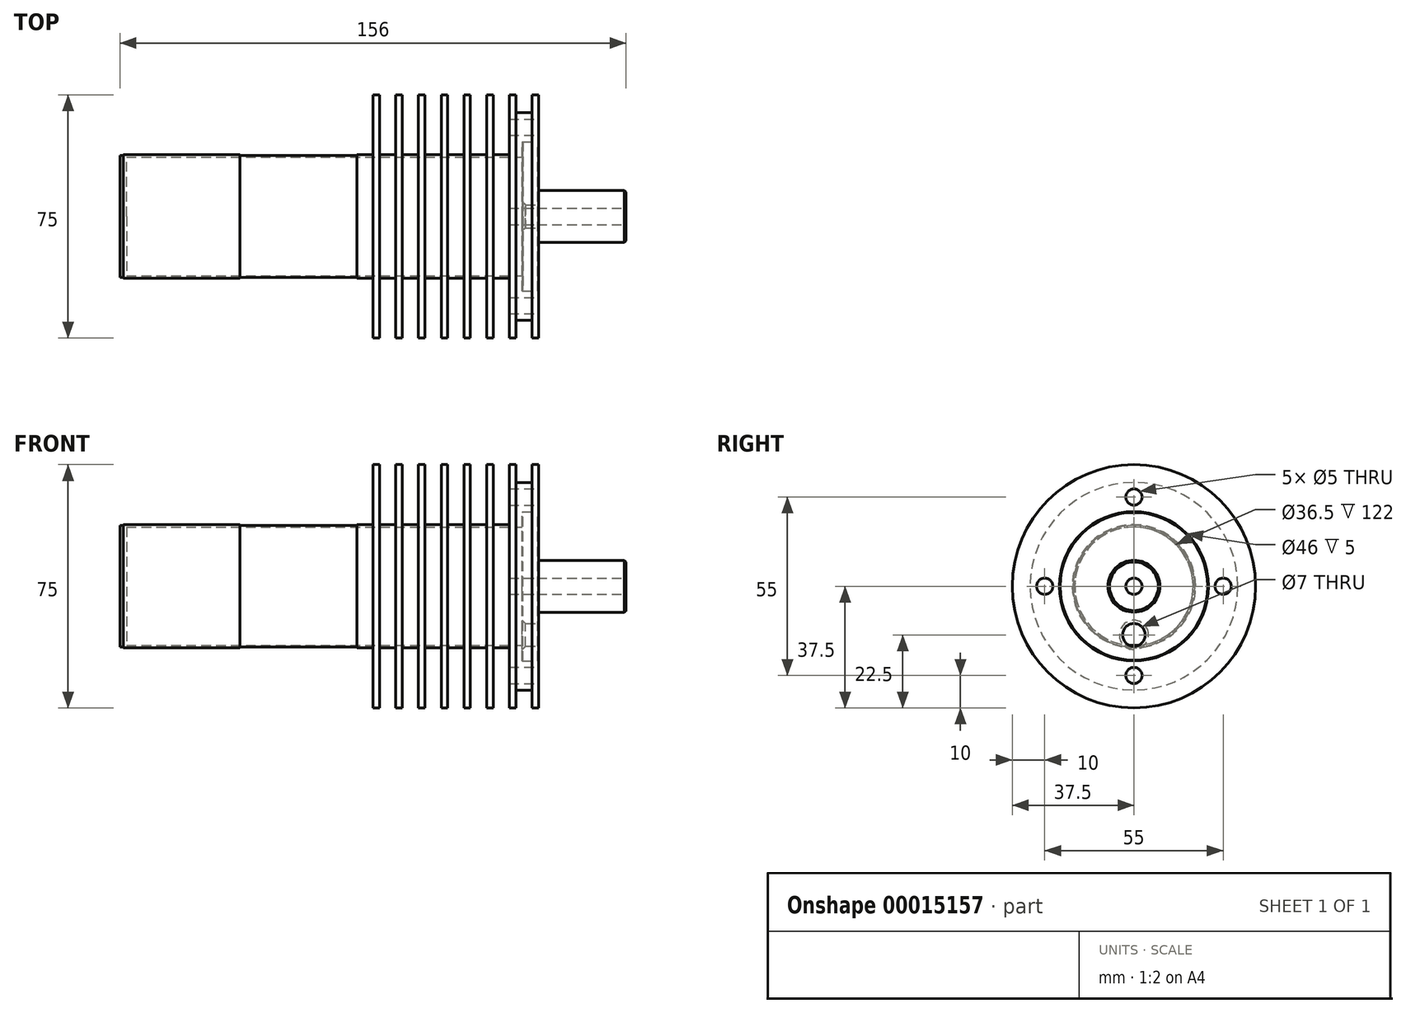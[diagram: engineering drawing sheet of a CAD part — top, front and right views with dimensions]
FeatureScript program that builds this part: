
annotation { "Feature Type Name" : "Feature", "Feature Type Description" : "" }
export const myFeature = defineFeature(function(context is Context, id is Id, definition is map)
    precondition{}
    {
        {
            var Q0;
            Q0=qCreatedBy(makeId("Front.planeOp"),FACE);
            var sketch = newSketch(context, id + "F0", { "sketchPlane" : qUnion([Q0])});
            skLineSegment(sketch, "E0.bottom", {"start": v(0, 0) * mm, "end": v(-128, 0) * mm});
            skLineSegment(sketch, "E0.top", {"start": v(-5, 18.25) * mm, "end": v(-56, 18.25) * mm});
            skLineSegment(sketch, "E0.left", {"start": v(0, 0) * mm, "end": v(0, 18.25) * mm, "construction": true});
            skLineSegment(sketch, "E0.right", {"start": v(-128, 0) * mm, "end": v(-128, 18.25) * mm, "construction": true});
            skLineSegment(sketch, "E1.top", {"start": v(-128, 19) * mm, "end": v(-92, 19) * mm});
            skLineSegment(sketch, "E1.left", {"start": v(-128, 18.25) * mm, "end": v(-128, 19) * mm});
            skLineSegment(sketch, "E1.right", {"start": v(-92, 18.75) * mm, "end": v(-92, 19) * mm});
            skLineSegment(sketch, "E2.bottom", {"start": v(-92, 18.25) * mm, "end": v(-56, 18.25) * mm});
            skLineSegment(sketch, "E2.top", {"start": v(-92, 18.75) * mm, "end": v(-56, 18.75) * mm});
            skLineSegment(sketch, "E3", {"start": v(-92, 18.25) * mm, "end": v(-128, 18.25) * mm});
            skLineSegment(sketch, "E4", {"start": v(-56, 19) * mm, "end": v(-51, 19) * mm});
            skLineSegment(sketch, "E5", {"start": v(-56, 18.75) * mm, "end": v(-56, 19) * mm});
            skLineSegment(sketch, "E6.bottom", {"start": v(-5, 18.25) * mm, "end": v(-51, 18.25) * mm});
            skLineSegment(sketch, "E6.top", {"start": v(0, 37.5) * mm, "end": v(-2, 37.5) * mm});
            skLineSegment(sketch, "E6.left", {"start": v(0, 23) * mm, "end": v(0, 37.5) * mm});
            skLineSegment(sketch, "E7", {"start": v(-9, 37.5) * mm, "end": v(-9, 19) * mm});
            skLineSegment(sketch, "E8.top", {"start": v(-7, 32) * mm, "end": v(-2, 32) * mm});
            skLineSegment(sketch, "E8.left", {"start": v(-7, 37.5) * mm, "end": v(-7, 32) * mm});
            skLineSegment(sketch, "E8.right", {"start": v(-2, 37.5) * mm, "end": v(-2, 32) * mm});
            skLineSegment(sketch, "E9.top", {"start": v(0, 23) * mm, "end": v(-5, 23) * mm});
            skLineSegment(sketch, "E9.right", {"start": v(-5, 18.25) * mm, "end": v(-5, 23) * mm});
            skLineSegment(sketch, "E10.bottom", {"start": v(-14, 37.5) * mm, "end": v(-16, 37.5) * mm});
            skLineSegment(sketch, "E10.left", {"start": v(-14, 37.5) * mm, "end": v(-14, 19) * mm});
            skLineSegment(sketch, "E10.right", {"start": v(-16, 37.5) * mm, "end": v(-16, 19) * mm});
            skLineSegment(sketch, "E11.1.0.0", {"start": v(-21, 37.5) * mm, "end": v(-21, 19) * mm});
            skLineSegment(sketch, "E11.1.0.1", {"start": v(-23, 37.5) * mm, "end": v(-23, 19) * mm});
            skLineSegment(sketch, "E11.2.0.0", {"start": v(-28, 37.5) * mm, "end": v(-28, 19) * mm});
            skLineSegment(sketch, "E11.2.0.1", {"start": v(-30, 37.5) * mm, "end": v(-30, 19) * mm});
            skLineSegment(sketch, "E11.3.0.0", {"start": v(-35, 37.5) * mm, "end": v(-35, 19) * mm});
            skLineSegment(sketch, "E11.3.0.1", {"start": v(-37, 37.5) * mm, "end": v(-37, 19) * mm});
            skLineSegment(sketch, "E11.4.0.0", {"start": v(-42, 37.5) * mm, "end": v(-42, 19) * mm});
            skLineSegment(sketch, "E11.4.0.1", {"start": v(-44, 37.5) * mm, "end": v(-44, 19) * mm});
            skLineSegment(sketch, "E11.5.0.0", {"start": v(-49, 37.5) * mm, "end": v(-49, 19) * mm});
            skLineSegment(sketch, "E11.5.0.1", {"start": v(-51, 37.5) * mm, "end": v(-51, 19) * mm});
            skLineSegment(sketch, "E11.direction1", {"start": v(-16, 19) * mm, "end": v(-21, 19) * mm, "construction": true});
            skLineSegment(sketch, "E12", {"start": v(0, 27.5) * mm, "end": v(-9, 27.5) * mm, "construction": true});
            skLineSegment(sketch, "E13.0", {"start": v(0, 30) * mm, "end": v(-9, 30) * mm, "construction": true});
            skLineSegment(sketch, "E14.0", {"start": v(0, 25) * mm, "end": v(-9, 25) * mm, "construction": true});
            skLineSegment(sketch, "E15.trimOffspring", {"start": v(-7, 37.5) * mm, "end": v(-9, 37.5) * mm});
            skLineSegment(sketch, "E16.trimOffspring", {"start": v(-21, 37.5) * mm, "end": v(-23, 37.5) * mm});
            skLineSegment(sketch, "E17.trimOffspring", {"start": v(-28, 37.5) * mm, "end": v(-30, 37.5) * mm});
            skLineSegment(sketch, "E18.trimOffspring", {"start": v(-35, 37.5) * mm, "end": v(-37, 37.5) * mm});
            skLineSegment(sketch, "E19.trimOffspring", {"start": v(-42, 37.5) * mm, "end": v(-44, 37.5) * mm});
            skLineSegment(sketch, "E20.trimOffspring", {"start": v(-49, 37.5) * mm, "end": v(-51, 37.5) * mm});
            skLineSegment(sketch, "E21.trimOffspring", {"start": v(-21, 19) * mm, "end": v(-16, 19) * mm});
            skLineSegment(sketch, "E22.trimOffspring", {"start": v(-28, 19) * mm, "end": v(-23, 19) * mm});
            skLineSegment(sketch, "E23.trimOffspring", {"start": v(-35, 19) * mm, "end": v(-30, 19) * mm});
            skLineSegment(sketch, "E24.trimOffspring", {"start": v(-42, 19) * mm, "end": v(-37, 19) * mm});
            skLineSegment(sketch, "E25.trimOffspring", {"start": v(-49, 19) * mm, "end": v(-44, 19) * mm});
            skLineSegment(sketch, "E26.trimOffspring", {"start": v(-14, 19) * mm, "end": v(-9, 19) * mm});
            skPoint(sketch, "E27.orphan", {"position": v(-91, 19) * mm});
            skPoint(sketch, "E28.orphan", {"position": v(-84, 19) * mm});
            skPoint(sketch, "E29.orphan", {"position": v(-77, 19) * mm});
            skPoint(sketch, "E30.orphan", {"position": v(-70, 19) * mm});
            skPoint(sketch, "E31.orphan", {"position": v(-63, 19) * mm});
            skLineSegment(sketch, "E32", {"start": v(-5, 18.25) * mm, "end": v(0, 18.25) * mm, "construction": true});
            skSolve(sketch);
        }
        {
            var Q0;
            Q0=makeQuery(id+"F0.imprint","IMPRINT",FACE,{"disambiguationData":[TD([[makeQuery(id+"F0.imprint","IMPRINT",EDGE,{"derivedFrom":sQuery(id+"F0.wireOp",EDGE,"E0.top")}),-1.0]])]});
            var Q1;
            Q1=sQuery(id+"F0.wireOp",EDGE,"E0.bottom");
            revolve(context, id + "F1", {"entities" : qUnion([Q0]), "axis" : qUnion([Q1]), "revolveType" : RevolveType.FULL});
        }
        {
            var Q0;
            Q0=makeQuery(id+"F1.opRevolve","SWEPT_FACE",FACE,{"disambiguationData":[OSD([sQuery(id+"F0.wireOp",EDGE,"E6.left")])]});
            var sketch = newSketch(context, id + "F2", { "sketchPlane" : qUnion([Q0])});
            skPoint(sketch, "E33.0", {"position": v(0, 0) * mm});
            skCircle(sketch, "E34", {"center": v(0, 0) * mm, "radius": 27.5 * mm, "construction": true});
            skLineSegment(sketch, "E35", {"start": v(0, 0) * mm, "end": v(27.5, 0) * mm, "construction": true});
            skCircle(sketch, "E36", {"center": v(27.5, 0) * mm, "radius": 2.5 * mm});
            skCircle(sketch, "E37.1.0", {"center": v(0, 27.5) * mm, "radius": 2.5 * mm});
            skCircle(sketch, "E37.2.0", {"center": v(-27.5, 0) * mm, "radius": 2.5 * mm});
            skCircle(sketch, "E37.3.0", {"center": v(0, -27.5) * mm, "radius": 2.5 * mm});
            skSolve(sketch);
        }
        {
            var Q0;
            Q0=makeQuery(id+"F2.imprint","IMPRINT",FACE,{"disambiguationData":[TD([[makeQuery(id+"F2.imprint","IMPRINT",EDGE,{"derivedFrom":sQuery(id+"F2.wireOp",EDGE,"E37.1.0")}),1.0]])]});
            var Q1;
            Q1=makeQuery(id+"F2.imprint","IMPRINT",FACE,{"disambiguationData":[TD([[makeQuery(id+"F2.imprint","IMPRINT",EDGE,{"derivedFrom":sQuery(id+"F2.wireOp",EDGE,"E36")}),1.0]])]});
            var Q2;
            Q2=makeQuery(id+"F2.imprint","IMPRINT",FACE,{"disambiguationData":[TD([[makeQuery(id+"F2.imprint","IMPRINT",EDGE,{"derivedFrom":sQuery(id+"F2.wireOp",EDGE,"E37.3.0")}),1.0]])]});
            var Q3;
            Q3=makeQuery(id+"F2.imprint","IMPRINT",FACE,{"disambiguationData":[TD([[makeQuery(id+"F2.imprint","IMPRINT",EDGE,{"derivedFrom":sQuery(id+"F2.wireOp",EDGE,"E37.2.0")}),1.0]])]});
            var Q4;
            Q4=makeQuery(id+"F1.opRevolve","SWEPT_FACE",FACE,{"disambiguationData":[OSD([sQuery(id+"F0.wireOp",EDGE,"E7")])]});
            extrude(context, id + "F3", {"entities" : qUnion([Q0, Q1, Q2, Q3]), "operationType" : NewBodyOperationType.REMOVE, "endBound" : BoundingType.UP_TO_SURFACE, "oppositeDirection" : true, "endBoundEntityFace" : qUnion([Q4]), "depth" : 25 * mm});
        }
        {
            var Q0;
            Q0=makeQuery(id+"F1.opRevolve","SWEPT_FACE",FACE,{"disambiguationData":[OSD([sQuery(id+"F0.wireOp",EDGE,"E1.left")])]});
            var sketch = newSketch(context, id + "F4", { "sketchPlane" : qUnion([Q0])});
            skCircle(sketch, "E38.0", {"center": v(0, 0) * mm, "radius": 18.25 * mm});
            skCircle(sketch, "E39", {"center": v(0, 0) * mm, "radius": 18.75 * mm});
            skSolve(sketch);
        }
        {
            var Q0;
            Q0=makeQuery(id+"F4.imprint","IMPRINT",FACE,{"disambiguationData":[TD([[makeQuery(id+"F4.imprint","IMPRINT",EDGE,{"derivedFrom":sQuery(id+"F4.wireOp",EDGE,"E38.0")}),-1.0]])]});
            extrude(context, id + "F5", {"entities" : qUnion([Q0]), "oppositeDirection" : true, "depth" : 1 * mm});
        }
        {
            var Q0;
            Q0=makeQuery(id+"F4.imprint","IMPRINT",FACE,{"disambiguationData":[TD([[makeQuery(id+"F4.imprint","IMPRINT",EDGE,{"derivedFrom":sQuery(id+"F4.wireOp",EDGE,"E38.0")}),-1.0]])]});
            var Q1;
            Q1=makeQuery(id+"F4.imprint","IMPRINT",FACE,{"disambiguationData":[TD([[makeQuery(id+"F4.imprint","IMPRINT",EDGE,{"derivedFrom":sQuery(id+"F4.wireOp",EDGE,"E38.0")}),1.0]])]});
            extrude(context, id + "F6", {"entities" : qUnion([Q0, Q1]), "operationType" : NewBodyOperationType.ADD, "depth" : 1 * mm});
        }
        {
            var Q0;
            Q0=makeQuery(id+"F1.opRevolve","SWEPT_FACE",FACE,{"disambiguationData":[OSD([sQuery(id+"F0.wireOp",EDGE,"E6.left")])]});
            var sketch = newSketch(context, id + "F7", { "sketchPlane" : qUnion([Q0])});
            skCircle(sketch, "E40.0", {"center": v(0, 0) * mm, "radius": 23 * mm});
            skCircle(sketch, "E41", {"center": v(0, 0) * mm, "radius": 2.5 * mm});
            skCircle(sketch, "E42", {"center": v(0, 0) * mm, "radius": 8 * mm});
            skCircle(sketch, "E43", {"center": v(0, -15) * mm, "radius": 3.5 * mm});
            skSolve(sketch);
        }
        {
            var Q0;
            Q0=makeQuery(id+"F7.imprint","IMPRINT",FACE,{"disambiguationData":[TD([[makeQuery(id+"F7.imprint","IMPRINT",EDGE,{"derivedFrom":sQuery(id+"F7.wireOp",EDGE,"E40.0")}),1.0]])]});
            var Q1;
            Q1=makeQuery(id+"F7.imprint","IMPRINT",FACE,{"disambiguationData":[TD([[makeQuery(id+"F7.imprint","IMPRINT",EDGE,{"derivedFrom":sQuery(id+"F7.wireOp",EDGE,"E41")}),-1.0]])]});
            extrude(context, id + "F8", {"entities" : qUnion([Q0, Q1]), "oppositeDirection" : true, "depth" : 5 * mm});
        }
        {
            var Q0;
            Q0=makeQuery(id+"F7.imprint","IMPRINT",FACE,{"disambiguationData":[TD([[makeQuery(id+"F7.imprint","IMPRINT",EDGE,{"derivedFrom":sQuery(id+"F7.wireOp",EDGE,"E41")}),-1.0]])]});
            extrude(context, id + "F9", {"entities" : qUnion([Q0]), "operationType" : NewBodyOperationType.ADD, "depth" : (32 - 5) * mm});
        }
        {
            var Q0;
            Q0=makeQuery(id+"F9.opExtrude","CAP_EDGE",EDGE,{"disambiguationData":[OSD([sQuery(id+"F7.wireOp",EDGE,"E42")])],"isStart":false});
            chamfer(context, id + "F10", {"entities" : qUnion([Q0]), "width" : .5 * mm, "tangentPropagation" : true});
        }
        {
            var Q0;
            Q0=makeQuery(id+"F8.opExtrude","CAP_EDGE",EDGE,{"disambiguationData":[OSD([sQuery(id+"F7.wireOp",EDGE,"E40.0")])],"isStart":false});
            var Q1;
            Q1=makeQuery(id+"F8.opExtrude","CAP_EDGE",EDGE,{"disambiguationData":[OSD([sQuery(id+"F7.wireOp",EDGE,"E40.0")])],"isStart":true});
            chamfer(context, id + "F11", {"entities" : qUnion([Q0, Q1]), "width" : .25 * mm, "tangentPropagation" : true});
        }
        {
            var Q0;
            Q0=makeQuery(id+"F8.opExtrude","CAP_EDGE",EDGE,{"disambiguationData":[OSD([sQuery(id+"F7.wireOp",EDGE,"E43")])],"isStart":false});
            chamfer(context, id + "F12", {"entities" : qUnion([Q0]), "width" : 1 * mm, "tangentPropagation" : true});
        }
    });
